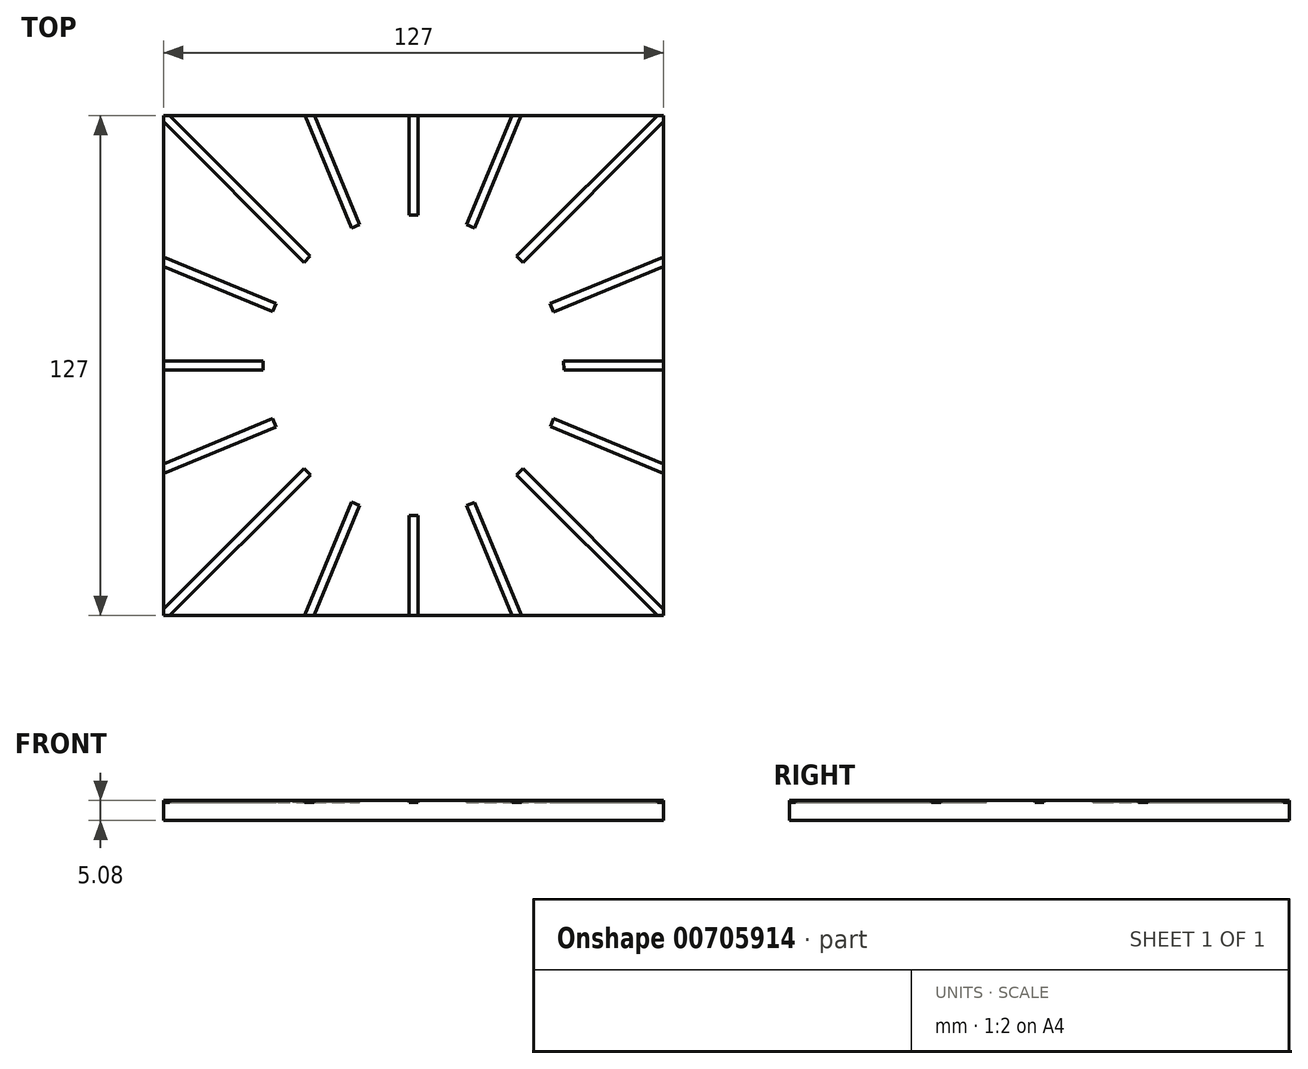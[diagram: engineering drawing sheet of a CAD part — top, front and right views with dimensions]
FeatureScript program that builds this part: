
annotation { "Feature Type Name" : "Feature", "Feature Type Description" : "" }
export const myFeature = defineFeature(function(context is Context, id is Id, definition is map)
    precondition{}
    {
        {
            var Q0;
            Q0=qCreatedBy(makeId("Top.planeOp"),FACE);
            var sketch = newSketch(context, id + "F0", { "sketchPlane" : qUnion([Q0])});
            skLineSegment(sketch, "E0.bottom", {"start": v(63.5, -63.5) * mm, "end": v(-63.5, -63.5) * mm});
            skLineSegment(sketch, "E0.top", {"start": v(63.5, 63.5) * mm, "end": v(-63.5, 63.5) * mm});
            skLineSegment(sketch, "E0.left", {"start": v(63.5, -63.5) * mm, "end": v(63.5, 63.5) * mm});
            skLineSegment(sketch, "E0.right", {"start": v(-63.5, -63.5) * mm, "end": v(-63.5, 63.5) * mm});
            skPoint(sketch, "E0.middle", {"position": v(0, 0) * mm});
            skSolve(sketch);
        }
        {
            var Q0;
            Q0 = qSketchRegion(id + "F0", true);
            extrude(context, id + "F1", {"entities" : qUnion([Q0]), "depth" : 5.08 * mm, "offsetDistance" : 25.4 * mm});
        }
        {
            var Q0;
            Q0=makeQuery(id+"F1.opExtrude","CAP_FACE",FACE,{"disambiguationData":[OSD([sQuery(id+"F0.wireOp",EDGE,"E0.bottom"),sQuery(id+"F0.wireOp",EDGE,"E0.top"),sQuery(id+"F0.wireOp",EDGE,"E0.left"),sQuery(id+"F0.wireOp",EDGE,"E0.right")])],"isStart":false});
            var sketch = newSketch(context, id + "F2", { "sketchPlane" : qUnion([Q0])});
            skLineSegment(sketch, "E1.right", {"start": v(90.22, -1.12) * mm, "end": v(90.22, 1.12) * mm});
            skPoint(sketch, "E1.middle", {"position": v(0, 0) * mm});
            skLineSegment(sketch, "E2.bottom", {"start": v(-1.1, -90.22) * mm, "end": v(1.1, -90.22) * mm});
            skLineSegment(sketch, "E2.top", {"start": v(-1.1, 90.22) * mm, "end": v(1.1, 90.22) * mm});
            skLineSegment(sketch, "E3", {"start": v(1.1, 90.22) * mm, "end": v(1.1, 38.17) * mm});
            skLineSegment(sketch, "E4", {"start": v(1.1, 38.17) * mm, "end": v(-1.1, 38.17) * mm});
            skLineSegment(sketch, "E5", {"start": v(-1.1, 38.17) * mm, "end": v(-1.1, 90.22) * mm});
            skLineSegment(sketch, "E6", {"start": v(90.22, -1.12) * mm, "end": v(38.17, -1.12) * mm});
            skLineSegment(sketch, "E7", {"start": v(38.17, -1.12) * mm, "end": v(38.14, 1.12) * mm});
            skLineSegment(sketch, "E8", {"start": v(38.14, 1.12) * mm, "end": v(90.22, 1.12) * mm});
            skLineSegment(sketch, "E9", {"start": v(1.1, -90.22) * mm, "end": v(1.1, -38.17) * mm});
            skLineSegment(sketch, "E10", {"start": v(1.1, -38.17) * mm, "end": v(-1.1, -38.17) * mm});
            skLineSegment(sketch, "E11", {"start": v(-1.1, -38.17) * mm, "end": v(-1.1, -90.22) * mm});
            skLineSegment(sketch, "E12", {"start": v(-90.22, 1.12) * mm, "end": v(-90.22, -1.12) * mm});
            skLineSegment(sketch, "E13", {"start": v(-90.22, -1.12) * mm, "end": v(-38.17, -1.12) * mm});
            skLineSegment(sketch, "E14", {"start": v(-38.17, -1.12) * mm, "end": v(-38.17, 1.12) * mm});
            skLineSegment(sketch, "E15", {"start": v(-38.17, 1.12) * mm, "end": v(-90.22, 1.12) * mm});
            skLineSegment(sketch, "E16.right", {"start": v(64.57, 63) * mm, "end": v(63, 64.58) * mm});
            skPoint(sketch, "E16.middle", {"position": v(-0.01, 0) * mm});
            skLineSegment(sketch, "E17.bottom", {"start": v(63, -64.57) * mm, "end": v(64.56, -63.02) * mm});
            skLineSegment(sketch, "E17.top", {"start": v(-64.58, 63.01) * mm, "end": v(-63.03, 64.56) * mm});
            skLineSegment(sketch, "E18", {"start": v(-63.03, 64.56) * mm, "end": v(-26.22, 27.76) * mm});
            skLineSegment(sketch, "E19", {"start": v(-26.22, 27.76) * mm, "end": v(-27.78, 26.2) * mm});
            skLineSegment(sketch, "E20", {"start": v(-27.78, 26.2) * mm, "end": v(-64.58, 63.01) * mm});
            skLineSegment(sketch, "E21", {"start": v(64.57, 63) * mm, "end": v(27.77, 26.2) * mm});
            skLineSegment(sketch, "E22", {"start": v(27.77, 26.2) * mm, "end": v(26.16, 27.75) * mm});
            skLineSegment(sketch, "E23", {"start": v(26.16, 27.75) * mm, "end": v(63, 64.58) * mm});
            skLineSegment(sketch, "E24", {"start": v(64.56, -63.02) * mm, "end": v(27.76, -26.22) * mm});
            skLineSegment(sketch, "E25", {"start": v(27.76, -26.22) * mm, "end": v(26.2, -27.77) * mm});
            skLineSegment(sketch, "E26", {"start": v(26.2, -27.77) * mm, "end": v(63, -64.57) * mm});
            skLineSegment(sketch, "E27", {"start": v(-64.6, -63) * mm, "end": v(-63.01, -64.59) * mm});
            skLineSegment(sketch, "E28", {"start": v(-63.01, -64.59) * mm, "end": v(-26.2, -27.79) * mm});
            skLineSegment(sketch, "E29", {"start": v(-26.2, -27.79) * mm, "end": v(-27.8, -26.2) * mm});
            skLineSegment(sketch, "E30", {"start": v(-27.8, -26.2) * mm, "end": v(-64.6, -63) * mm});
            skLineSegment(sketch, "E31.right", {"start": v(83.7, 33.54) * mm, "end": v(82.84, 35.61) * mm});
            skPoint(sketch, "E31.middle", {"position": v(-0.08, 0.05) * mm});
            skLineSegment(sketch, "E32.bottom", {"start": v(33.43, -83.72) * mm, "end": v(35.46, -82.88) * mm});
            skLineSegment(sketch, "E32.top", {"start": v(-35.62, 82.98) * mm, "end": v(-33.59, 83.82) * mm});
            skLineSegment(sketch, "E33", {"start": v(-33.59, 83.82) * mm, "end": v(-13.67, 35.74) * mm});
            skLineSegment(sketch, "E34", {"start": v(-13.67, 35.74) * mm, "end": v(-15.7, 34.9) * mm});
            skLineSegment(sketch, "E35", {"start": v(-15.7, 34.9) * mm, "end": v(-35.62, 82.98) * mm});
            skLineSegment(sketch, "E36", {"start": v(83.7, 33.54) * mm, "end": v(35.61, 13.62) * mm});
            skLineSegment(sketch, "E37", {"start": v(35.61, 13.62) * mm, "end": v(34.73, 15.68) * mm});
            skLineSegment(sketch, "E38", {"start": v(34.73, 15.68) * mm, "end": v(82.84, 35.61) * mm});
            skLineSegment(sketch, "E39", {"start": v(35.46, -82.88) * mm, "end": v(15.54, -34.8) * mm});
            skLineSegment(sketch, "E40", {"start": v(15.54, -34.8) * mm, "end": v(13.51, -35.63) * mm});
            skLineSegment(sketch, "E41", {"start": v(13.51, -35.63) * mm, "end": v(33.43, -83.72) * mm});
            skLineSegment(sketch, "E42", {"start": v(-83.86, -33.44) * mm, "end": v(-83, -35.5) * mm});
            skLineSegment(sketch, "E43", {"start": v(-83, -35.5) * mm, "end": v(-34.91, -15.59) * mm});
            skLineSegment(sketch, "E44", {"start": v(-34.91, -15.59) * mm, "end": v(-35.77, -13.52) * mm});
            skLineSegment(sketch, "E45", {"start": v(-35.77, -13.52) * mm, "end": v(-83.86, -33.44) * mm});
            skLineSegment(sketch, "E46.right", {"start": v(82.82, -35.45) * mm, "end": v(83.67, -33.38) * mm});
            skPoint(sketch, "E46.middle", {"position": v(-0.1, 0.1) * mm});
            skLineSegment(sketch, "E47.bottom", {"start": v(-35.64, -82.82) * mm, "end": v(-33.61, -83.66) * mm});
            skLineSegment(sketch, "E47.top", {"start": v(33.4, 83.88) * mm, "end": v(35.43, 83.04) * mm});
            skLineSegment(sketch, "E48", {"start": v(35.43, 83.04) * mm, "end": v(15.52, 34.95) * mm});
            skLineSegment(sketch, "E49", {"start": v(15.52, 34.95) * mm, "end": v(13.49, 35.8) * mm});
            skLineSegment(sketch, "E50", {"start": v(13.49, 35.8) * mm, "end": v(33.4, 83.88) * mm});
            skLineSegment(sketch, "E51", {"start": v(82.82, -35.45) * mm, "end": v(34.73, -15.53) * mm});
            skLineSegment(sketch, "E52", {"start": v(34.73, -15.53) * mm, "end": v(35.56, -13.45) * mm});
            skLineSegment(sketch, "E53", {"start": v(35.56, -13.45) * mm, "end": v(83.67, -33.38) * mm});
            skLineSegment(sketch, "E54", {"start": v(-33.61, -83.66) * mm, "end": v(-13.7, -35.58) * mm});
            skLineSegment(sketch, "E55", {"start": v(-13.7, -35.58) * mm, "end": v(-15.72, -34.74) * mm});
            skLineSegment(sketch, "E56", {"start": v(-15.72, -34.74) * mm, "end": v(-35.64, -82.82) * mm});
            skLineSegment(sketch, "E57", {"start": v(-83.02, 35.67) * mm, "end": v(-83.88, 33.6) * mm});
            skLineSegment(sketch, "E58", {"start": v(-83.88, 33.6) * mm, "end": v(-35.8, 13.68) * mm});
            skLineSegment(sketch, "E59", {"start": v(-35.8, 13.68) * mm, "end": v(-34.94, 15.75) * mm});
            skLineSegment(sketch, "E60", {"start": v(-34.94, 15.75) * mm, "end": v(-83.02, 35.67) * mm});
            skSolve(sketch);
        }
        {
            var Q0;
            Q0 = qSketchRegion(id + "F2", true);
            extrude(context, id + "F3", {"entities" : qUnion([Q0]), "operationType" : NewBodyOperationType.REMOVE, "oppositeDirection" : true, "depth" : 0.5 * mm, "offsetDistance" : 25.4 * mm});
        }
    });
